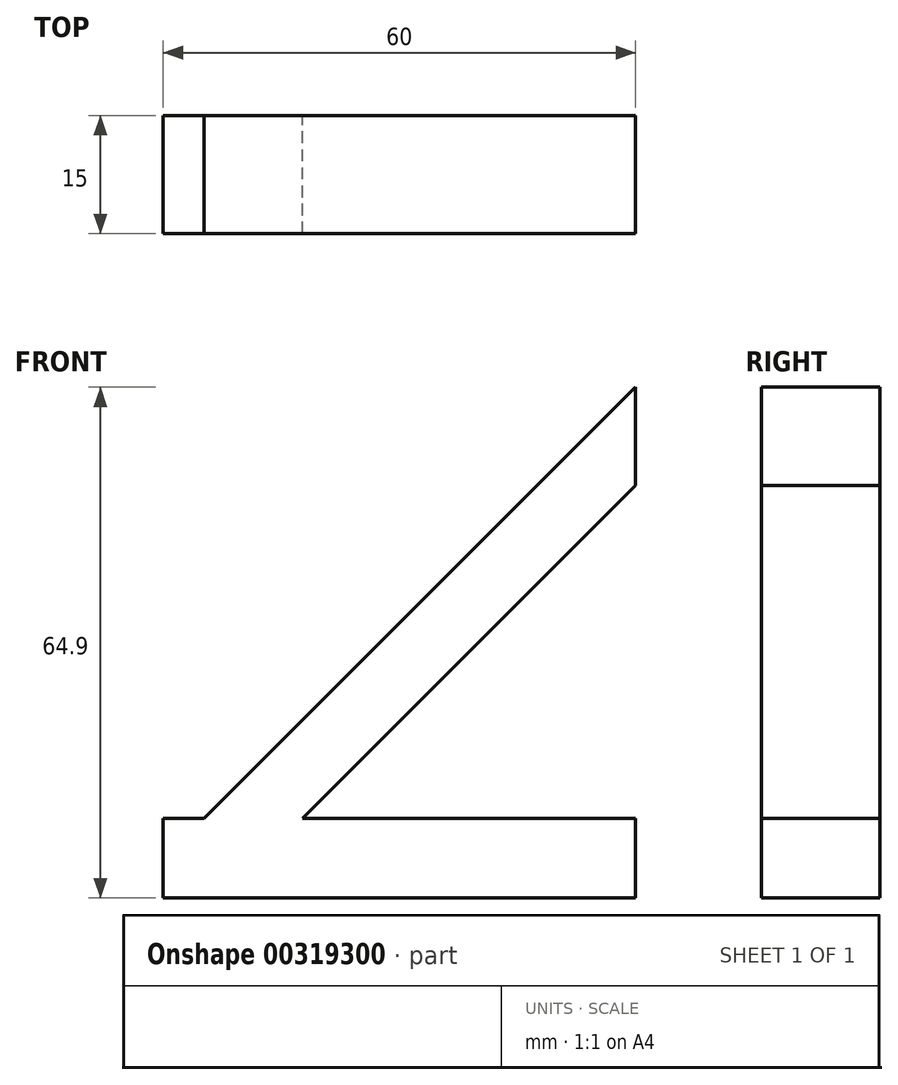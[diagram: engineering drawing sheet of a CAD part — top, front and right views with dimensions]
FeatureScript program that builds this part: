
annotation { "Feature Type Name" : "Feature", "Feature Type Description" : "" }
export const myFeature = defineFeature(function(context is Context, id is Id, definition is map)
    precondition{}
    {
        {
            var Q0;
            Q0=qCreatedBy(makeId("Front.planeOp"),FACE);
            var sketch = newSketch(context, id + "F0", { "sketchPlane" : qUnion([Q0])});
            skLineSegment(sketch, "E0", {"start": v(0, 54.8) * mm, "end": v(-54.8, 0) * mm});
            skLineSegment(sketch, "E1", {"start": v(-54.8, 0) * mm, "end": v(-42.3, 0) * mm});
            skLineSegment(sketch, "E2", {"start": v(-42.3, 0) * mm, "end": v(0, 42.3) * mm});
            skLineSegment(sketch, "E3", {"start": v(0, 54.8) * mm, "end": v(0, 42.3) * mm});
            skLineSegment(sketch, "E4", {"start": v(-60, 0) * mm, "end": v(0, 0) * mm});
            skLineSegment(sketch, "E5", {"start": v(0, 0) * mm, "end": v(0, -10.1) * mm});
            skLineSegment(sketch, "E6", {"start": v(0, -10.1) * mm, "end": v(-60, -10.1) * mm});
            skLineSegment(sketch, "E7", {"start": v(-60, -10.1) * mm, "end": v(-60, 0) * mm});
            skSolve(sketch);
        }
        {
            var Q0;
            Q0 = qSketchRegion(id + "F0", true);
            extrude(context, id + "F1", {"entities" : qUnion([Q0]), "depth" : 15 * mm});
        }
    });
